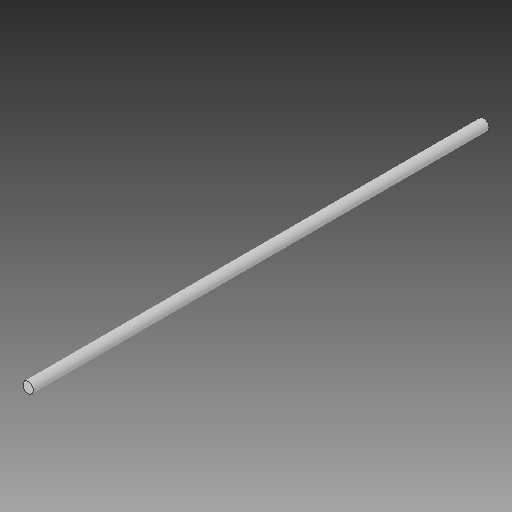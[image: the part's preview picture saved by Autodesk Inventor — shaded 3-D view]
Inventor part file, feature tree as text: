
AUTODESK INVENTOR PART (.ipt)
format: ipt  version: 2017 (Build 210142000, 142)  size: 87,040 bytes
history: native  units: in
note: dims shown in document units (in); Inventor stores cm internally (conversion verified against a paired STEP export)
features: extrude x1, sketch x1
ambient origin geometry x8: Origin, YZ Plane, XZ Plane, XY Plane, X Axis, Y Axis, Z Axis, Center Point
bodies: Solid1 (feature_tree)
feature tree (2):
  extrude  "Extrusion1"  Depth=8.0in TaperAngle=0.0deg
  sketch  "Sketch1"  dims[d0=0.188in d1=8.0in d2=0.0in]
